# Revit family: S261XBODY_ZV-1966
name_source: partatom
category: Plumbing Fixtures
units: mm (PartAtom-declared; Revit-internal decimal feet)

## family parameters
Cut with Voids When Loaded = No
Host = Face
OmniClass Number = 23.65.55.00
OmniClass Title = Distribution of Supplied Liquids/Gases
Part Type = Normal
Room Calculation Point = No
Round Connector Dimension = Use Diameter
Shared = No

## types (2) — shared parameters
Date Modified = January 30, 2015
Equipment Abbreviation = SVS
Family Version = 1.0
Manufacturer = Symmons Industries, Inc.
Model Disclaimer = Contact Symmons Industries, Inc. For More Information
Product Documentation Link = http://www.symmons.com
Product Page URL = http://www.symmons.com
URL = http://www.symmons.com
zz Text 1 = None Selected
zz Text 2 = None Selected
zero-valued in all types: Default Elevation

## per-type parameters (varying)
| type | Description | Model | Product Material |
| Chrome | Shower Valve System with Symmons Temptrol mixing valve,Chrome | 3500-CYL-B | Chrome - Symmons - Polished |
| Satin Nickel | Shower Valve System with Symmons Temptrol mixing valve, Satin Nickel | 3500-CYL-B-STN | Nickel - Symmons - Satin |

## geometry (parser evidence)
native form markers: Blend x8, Sweep x1
no freeform markers — native parametric forms only
